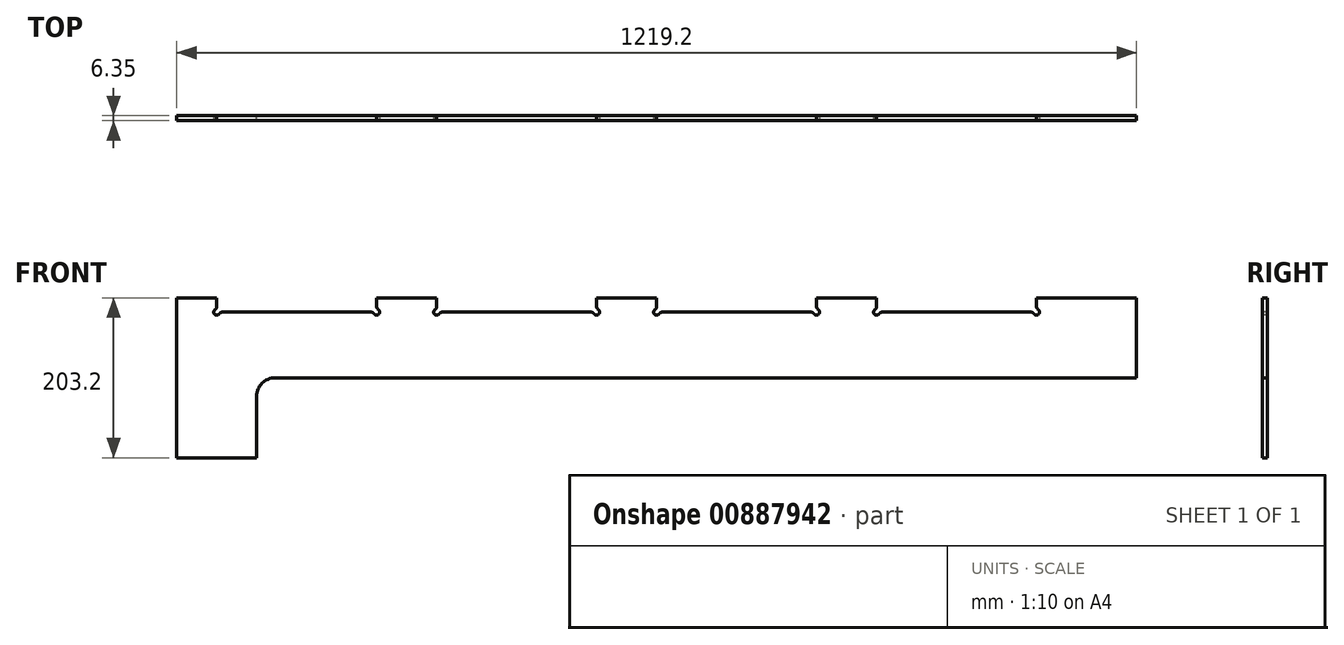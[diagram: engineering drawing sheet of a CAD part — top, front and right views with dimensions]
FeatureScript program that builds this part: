
annotation { "Feature Type Name" : "Feature", "Feature Type Description" : "" }
export const myFeature = defineFeature(function(context is Context, id is Id, definition is map)
    precondition{}
    {
        {
            var Q0;
            Q0=qCreatedBy(makeId("Front.planeOp"),FACE);
            var sketch = newSketch(context, id + "F0", { "sketchPlane" : qUnion([Q0])});
            skLineSegment(sketch, "E0", {"start": v(0, 0) * mm, "end": v(0, 203.2) * mm});
            skLineSegment(sketch, "E1", {"start": v(0, 203.2) * mm, "end": v(1219.2, 203.2) * mm});
            skLineSegment(sketch, "E2", {"start": v(1219.2, 203.2) * mm, "end": v(1219.2, 101.6) * mm});
            skLineSegment(sketch, "E3", {"start": v(1219.2, 101.6) * mm, "end": v(101.6, 101.6) * mm});
            skLineSegment(sketch, "E4", {"start": v(101.6, 101.6) * mm, "end": v(101.6, 0) * mm});
            skLineSegment(sketch, "E5", {"start": v(101.6, 0) * mm, "end": v(0, 0) * mm});
            skSolve(sketch);
        }
        {
            var Q0;
            Q0 = qSketchRegion(id + "F0", true);
            extrude(context, id + "F1", {"entities" : qUnion([Q0]), "depth" : 6.35 * mm, "offsetDistance" : 25.4 * mm});
        }
        {
            var Q0;
            Q0=makeQuery(id+"F1.opExtrude","CAP_FACE",FACE,{"disambiguationData":[OSD([sQuery(id+"F0.wireOp",EDGE,"E0"),sQuery(id+"F0.wireOp",EDGE,"E1"),sQuery(id+"F0.wireOp",EDGE,"E2"),sQuery(id+"F0.wireOp",EDGE,"E3"),sQuery(id+"F0.wireOp",EDGE,"E4"),sQuery(id+"F0.wireOp",EDGE,"E5")])],"isStart":false});
            var sketch = newSketch(context, id + "F2", { "sketchPlane" : qUnion([Q0])});
            skLineSegment(sketch, "E6", {"start": v(50.8, 203.2) * mm, "end": v(50.8, 184.99) * mm});
            skLineSegment(sketch, "E7", {"start": v(50.8, 184.99) * mm, "end": v(152.4, 184.99) * mm});
            skLineSegment(sketch, "E8", {"start": v(152.4, 184.99) * mm, "end": v(254, 184.99) * mm});
            skLineSegment(sketch, "E9", {"start": v(254, 184.99) * mm, "end": v(254, 203.2) * mm});
            skArc(sketch, "E10", {"start": v(54.6, 184.99) * mm, "mid": v(48.1, 182.3) * mm, "end": v(50.8, 188.8) * mm});
            skArc(sketch, "E11", {"start": v(250.2, 184.99) * mm, "mid": v(256.7, 182.3) * mm, "end": v(254, 188.8) * mm});
            skLineSegment(sketch, "E12", {"start": v(330.2, 203.2) * mm, "end": v(330.2, 184.99) * mm});
            skLineSegment(sketch, "E13", {"start": v(330.2, 184.99) * mm, "end": v(431.8, 184.99) * mm});
            skLineSegment(sketch, "E14", {"start": v(431.8, 184.99) * mm, "end": v(533.4, 184.99) * mm});
            skLineSegment(sketch, "E15", {"start": v(533.4, 184.99) * mm, "end": v(533.4, 203.2) * mm});
            skArc(sketch, "E16", {"start": v(529.6, 184.99) * mm, "mid": v(536.1, 182.3) * mm, "end": v(533.4, 188.8) * mm});
            skArc(sketch, "E17", {"start": v(330.2, 188.8) * mm, "mid": v(327.5, 182.3) * mm, "end": v(334, 184.99) * mm});
            skLineSegment(sketch, "E18", {"start": v(609.6, 203.2) * mm, "end": v(609.6, 184.99) * mm});
            skLineSegment(sketch, "E19", {"start": v(609.6, 184.99) * mm, "end": v(711.2, 184.99) * mm});
            skLineSegment(sketch, "E20", {"start": v(711.2, 184.99) * mm, "end": v(812.8, 184.99) * mm});
            skLineSegment(sketch, "E21", {"start": v(812.8, 184.99) * mm, "end": v(812.8, 203.2) * mm});
            skLineSegment(sketch, "E22", {"start": v(889, 203.2) * mm, "end": v(889, 184.99) * mm});
            skLineSegment(sketch, "E23", {"start": v(889, 184.99) * mm, "end": v(990.6, 184.99) * mm});
            skLineSegment(sketch, "E24", {"start": v(990.6, 184.99) * mm, "end": v(1092.2, 184.99) * mm});
            skLineSegment(sketch, "E25", {"start": v(1092.2, 184.99) * mm, "end": v(1092.2, 203.2) * mm});
            skArc(sketch, "E26", {"start": v(609.6, 188.8) * mm, "mid": v(606.9, 182.3) * mm, "end": v(613.4, 184.99) * mm});
            skArc(sketch, "E27", {"start": v(809, 184.99) * mm, "mid": v(815.5, 182.3) * mm, "end": v(812.8, 188.8) * mm});
            skArc(sketch, "E28", {"start": v(889, 188.8) * mm, "mid": v(886.3, 182.3) * mm, "end": v(892.8, 184.99) * mm});
            skArc(sketch, "E29", {"start": v(1088.39, 184.99) * mm, "mid": v(1094.9, 182.3) * mm, "end": v(1092.2, 188.8) * mm});
            skSolve(sketch);
        }
        {
            var Q0;
            Q0 = qSketchRegion(id + "F2", true);
            var Q1;
            {var subQ5=sQuery(id+"F2.wireOp",EDGE,"E6");var subQ8=makeQuery(id+"F1.opExtrude","CAP_EDGE",EDGE,{"disambiguationData":[OSD([sQuery(id+"F0.wireOp",EDGE,"E1")])],"isStart":false});var subQ9=makeQuery(id+"F2.imprint","INTERSECT",VERTEX,{"derivedFrom":[subQ8,subQ5]});Q1=makeQuery(id+"F2.imprint","IMPRINT",FACE,{"disambiguationData":[TD([[makeQuery(id+"F2.imprint","IMPRINT",EDGE,{"disambiguationData":[TD([[subQ9,-1.0]])],"derivedFrom":subQ5}),1.0]])]});}
            var Q2;
            {var subQ5=sQuery(id+"F2.wireOp",EDGE,"E12");var subQ8=makeQuery(id+"F1.opExtrude","CAP_EDGE",EDGE,{"disambiguationData":[OSD([sQuery(id+"F0.wireOp",EDGE,"E1")])],"isStart":false});var subQ9=makeQuery(id+"F2.imprint","INTERSECT",VERTEX,{"derivedFrom":[subQ8,subQ5]});Q2=makeQuery(id+"F2.imprint","IMPRINT",FACE,{"disambiguationData":[TD([[makeQuery(id+"F2.imprint","IMPRINT",EDGE,{"disambiguationData":[TD([[subQ9,-1.0]])],"derivedFrom":subQ5}),1.0]])]});}
            var Q3;
            {var subQ5=sQuery(id+"F2.wireOp",EDGE,"E18");var subQ8=makeQuery(id+"F1.opExtrude","CAP_EDGE",EDGE,{"disambiguationData":[OSD([sQuery(id+"F0.wireOp",EDGE,"E1")])],"isStart":false});var subQ9=makeQuery(id+"F2.imprint","INTERSECT",VERTEX,{"derivedFrom":[subQ8,subQ5]});Q3=makeQuery(id+"F2.imprint","IMPRINT",FACE,{"disambiguationData":[TD([[makeQuery(id+"F2.imprint","IMPRINT",EDGE,{"disambiguationData":[TD([[subQ9,-1.0]])],"derivedFrom":subQ5}),1.0]])]});}
            var Q4;
            {var subQ5=sQuery(id+"F2.wireOp",EDGE,"E22");var subQ6=makeQuery(id+"F1.opExtrude","CAP_EDGE",EDGE,{"disambiguationData":[OSD([sQuery(id+"F0.wireOp",EDGE,"E1")])],"isStart":false});var subQ7=makeQuery(id+"F2.imprint","INTERSECT",VERTEX,{"derivedFrom":[subQ6,subQ5]});Q4=makeQuery(id+"F2.imprint","IMPRINT",FACE,{"disambiguationData":[TD([[makeQuery(id+"F2.imprint","IMPRINT",EDGE,{"disambiguationData":[TD([[subQ7,-1.0]])],"derivedFrom":subQ5}),1.0]])]});}
            extrude(context, id + "F3", {"entities" : qUnion([Q0, Q1, Q2, Q3, Q4]), "operationType" : NewBodyOperationType.REMOVE, "endBound" : BoundingType.THROUGH_ALL, "oppositeDirection" : true, "depth" : 25.4 * mm, "offsetDistance" : 25.4 * mm});
        }
        {
            var Q0;
            Q0=makeQuery(id+"F3.boolean.opBoolean","COPY",EDGE,{"derivedFrom":makeQuery(id+"F3.opExtrude","SWEPT_EDGE",EDGE,{"disambiguationData":[OSD([sQuery(id+"F2.wireOp",EDGE,"E13"),sQuery(id+"F2.wireOp",EDGE,"E17")])]})});
            var Q1;
            Q1=makeQuery(id+"F3.boolean.opBoolean","COPY",EDGE,{"derivedFrom":makeQuery(id+"F3.opExtrude","SWEPT_EDGE",EDGE,{"disambiguationData":[OSD([sQuery(id+"F2.wireOp",EDGE,"E12"),sQuery(id+"F2.wireOp",EDGE,"E17")])]})});
            var Q2;
            Q2=makeQuery(id+"F3.boolean.opBoolean","COPY",EDGE,{"derivedFrom":makeQuery(id+"F3.opExtrude","SWEPT_EDGE",EDGE,{"disambiguationData":[OSD([sQuery(id+"F2.wireOp",EDGE,"E14"),sQuery(id+"F2.wireOp",EDGE,"E16")])]})});
            var Q3;
            Q3=makeQuery(id+"F3.boolean.opBoolean","COPY",EDGE,{"derivedFrom":makeQuery(id+"F3.opExtrude","SWEPT_EDGE",EDGE,{"disambiguationData":[OSD([sQuery(id+"F2.wireOp",EDGE,"E15"),sQuery(id+"F2.wireOp",EDGE,"E16")])]})});
            var Q4;
            Q4=makeQuery(id+"F3.boolean.opBoolean","COPY",EDGE,{"derivedFrom":makeQuery(id+"F3.opExtrude","SWEPT_EDGE",EDGE,{"disambiguationData":[OSD([sQuery(id+"F2.wireOp",EDGE,"E7"),sQuery(id+"F2.wireOp",EDGE,"E10")])]})});
            var Q5;
            Q5=makeQuery(id+"F3.boolean.opBoolean","COPY",EDGE,{"derivedFrom":makeQuery(id+"F3.opExtrude","SWEPT_EDGE",EDGE,{"disambiguationData":[OSD([sQuery(id+"F2.wireOp",EDGE,"E6"),sQuery(id+"F2.wireOp",EDGE,"E10")])]})});
            var Q6;
            Q6=makeQuery(id+"F3.boolean.opBoolean","COPY",EDGE,{"derivedFrom":makeQuery(id+"F3.opExtrude","SWEPT_EDGE",EDGE,{"disambiguationData":[OSD([sQuery(id+"F2.wireOp",EDGE,"E8"),sQuery(id+"F2.wireOp",EDGE,"E11")])]})});
            var Q7;
            Q7=makeQuery(id+"F3.boolean.opBoolean","COPY",EDGE,{"derivedFrom":makeQuery(id+"F3.opExtrude","SWEPT_EDGE",EDGE,{"disambiguationData":[OSD([sQuery(id+"F2.wireOp",EDGE,"E9"),sQuery(id+"F2.wireOp",EDGE,"E11")])]})});
            var Q8;
            Q8=makeQuery(id+"F3.boolean.opBoolean","COPY",EDGE,{"derivedFrom":makeQuery(id+"F3.opExtrude","SWEPT_EDGE",EDGE,{"disambiguationData":[OSD([sQuery(id+"F2.wireOp",EDGE,"E25"),sQuery(id+"F2.wireOp",EDGE,"E29")])]})});
            var Q9;
            Q9=makeQuery(id+"F3.boolean.opBoolean","COPY",EDGE,{"derivedFrom":makeQuery(id+"F3.opExtrude","SWEPT_EDGE",EDGE,{"disambiguationData":[OSD([sQuery(id+"F2.wireOp",EDGE,"E24"),sQuery(id+"F2.wireOp",EDGE,"E29")])]})});
            var Q10;
            Q10=makeQuery(id+"F3.boolean.opBoolean","COPY",EDGE,{"derivedFrom":makeQuery(id+"F3.opExtrude","SWEPT_EDGE",EDGE,{"disambiguationData":[OSD([sQuery(id+"F2.wireOp",EDGE,"E21"),sQuery(id+"F2.wireOp",EDGE,"E27")])]})});
            var Q11;
            Q11=makeQuery(id+"F3.boolean.opBoolean","COPY",EDGE,{"derivedFrom":makeQuery(id+"F3.opExtrude","SWEPT_EDGE",EDGE,{"disambiguationData":[OSD([sQuery(id+"F2.wireOp",EDGE,"E20"),sQuery(id+"F2.wireOp",EDGE,"E27")])]})});
            var Q12;
            Q12=makeQuery(id+"F3.boolean.opBoolean","COPY",EDGE,{"derivedFrom":makeQuery(id+"F3.opExtrude","SWEPT_EDGE",EDGE,{"disambiguationData":[OSD([sQuery(id+"F2.wireOp",EDGE,"E18"),sQuery(id+"F2.wireOp",EDGE,"E26")])]})});
            var Q13;
            Q13=makeQuery(id+"F3.boolean.opBoolean","COPY",EDGE,{"derivedFrom":makeQuery(id+"F3.opExtrude","SWEPT_EDGE",EDGE,{"disambiguationData":[OSD([sQuery(id+"F2.wireOp",EDGE,"E19"),sQuery(id+"F2.wireOp",EDGE,"E26")])]})});
            var Q14;
            Q14=makeQuery(id+"F3.boolean.opBoolean","COPY",EDGE,{"derivedFrom":makeQuery(id+"F3.opExtrude","SWEPT_EDGE",EDGE,{"disambiguationData":[OSD([sQuery(id+"F2.wireOp",EDGE,"E22"),sQuery(id+"F2.wireOp",EDGE,"E28")])]})});
            var Q15;
            Q15=makeQuery(id+"F3.boolean.opBoolean","COPY",EDGE,{"derivedFrom":makeQuery(id+"F3.opExtrude","SWEPT_EDGE",EDGE,{"disambiguationData":[OSD([sQuery(id+"F2.wireOp",EDGE,"E23"),sQuery(id+"F2.wireOp",EDGE,"E28")])]})});
            fillet(context, id + "F4", {"entities" : qUnion([Q0, Q1, Q2, Q3, Q4, Q5, Q6, Q7, Q8, Q9, Q10, Q11, Q12, Q13, Q14, Q15]), "radius" : 5.08 * mm, "tangentPropagation" : true, "allowEdgeOverflow" : false});
        }
        {
            var Q0;
            Q0=makeQuery(id+"F1.opExtrude","SWEPT_EDGE",EDGE,{"disambiguationData":[OSD([sQuery(id+"F0.wireOp",EDGE,"E3"),sQuery(id+"F0.wireOp",EDGE,"E4")])]});
            fillet(context, id + "F5", {"entities" : qUnion([Q0]), "radius" : 23.3 * mm, "tangentPropagation" : true, "allowEdgeOverflow" : false});
        }
    });
